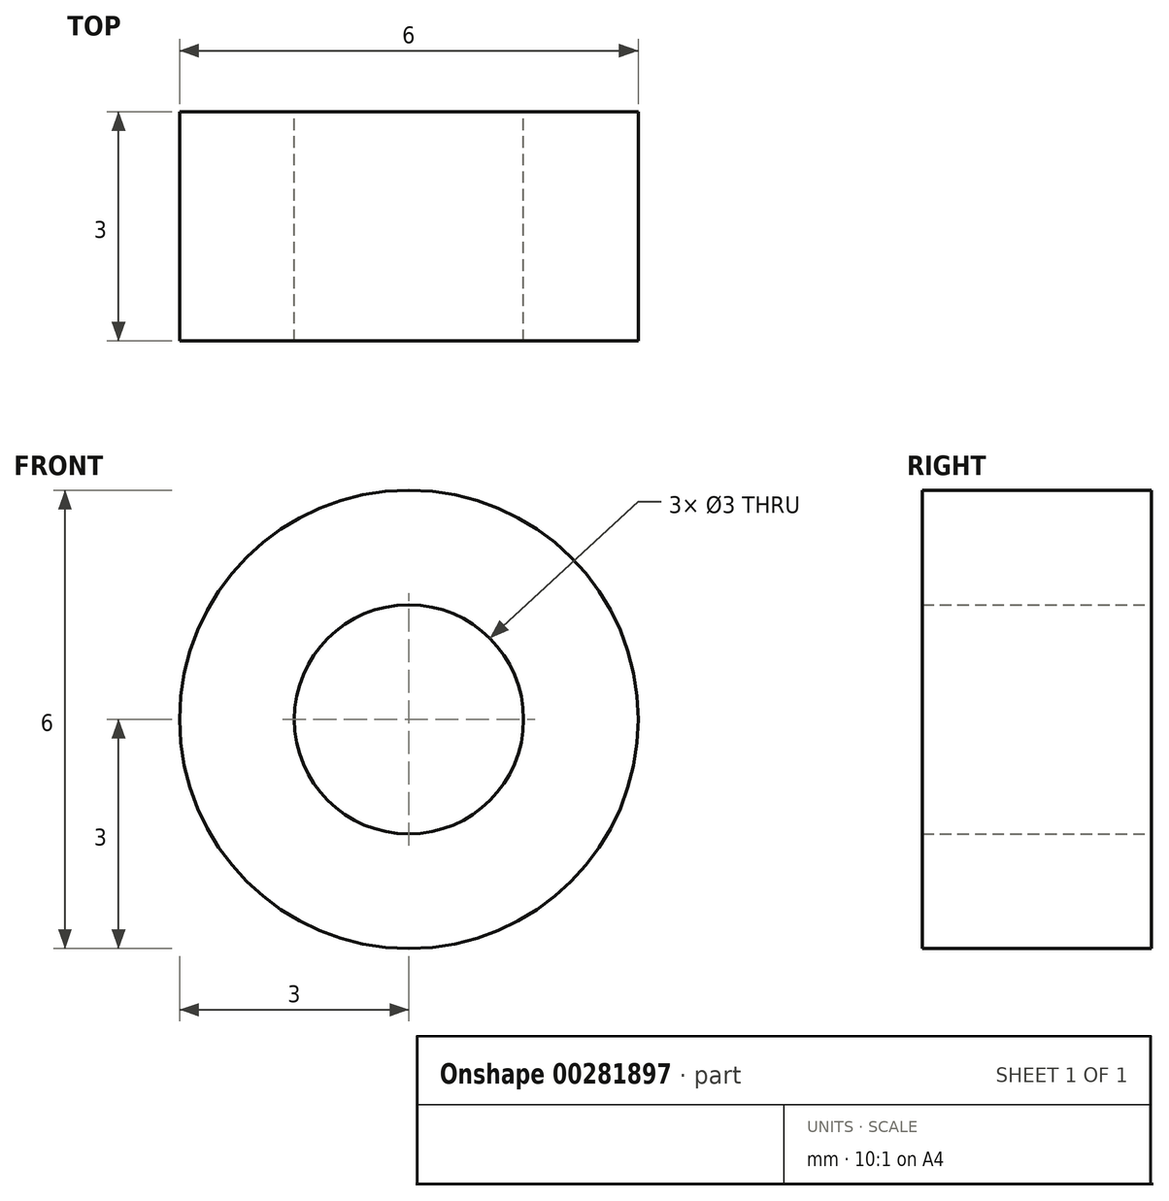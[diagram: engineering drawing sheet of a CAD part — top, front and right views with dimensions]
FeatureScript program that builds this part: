
annotation { "Feature Type Name" : "Feature", "Feature Type Description" : "" }
export const myFeature = defineFeature(function(context is Context, id is Id, definition is map)
    precondition{}
    {
        {
            var Q0;
            Q0=qCreatedBy(makeId("Front.planeOp"),FACE);
            var sketch = newSketch(context, id + "F0", { "sketchPlane" : qUnion([Q0])});
            skCircle(sketch, "E0", {"center": v(0, 0) * mm, "radius": 1.5 * mm});
            skCircle(sketch, "E1", {"center": v(0, 0) * mm, "radius": 3 * mm});
            skSolve(sketch);
        }
        {
            var Q0;
            Q0=qSketchRegion(id+"F0",true);
            extrude(context, id + "F1", {"entities" : qUnion([Q0]), "depth" : 3 * mm});
        }
    });
